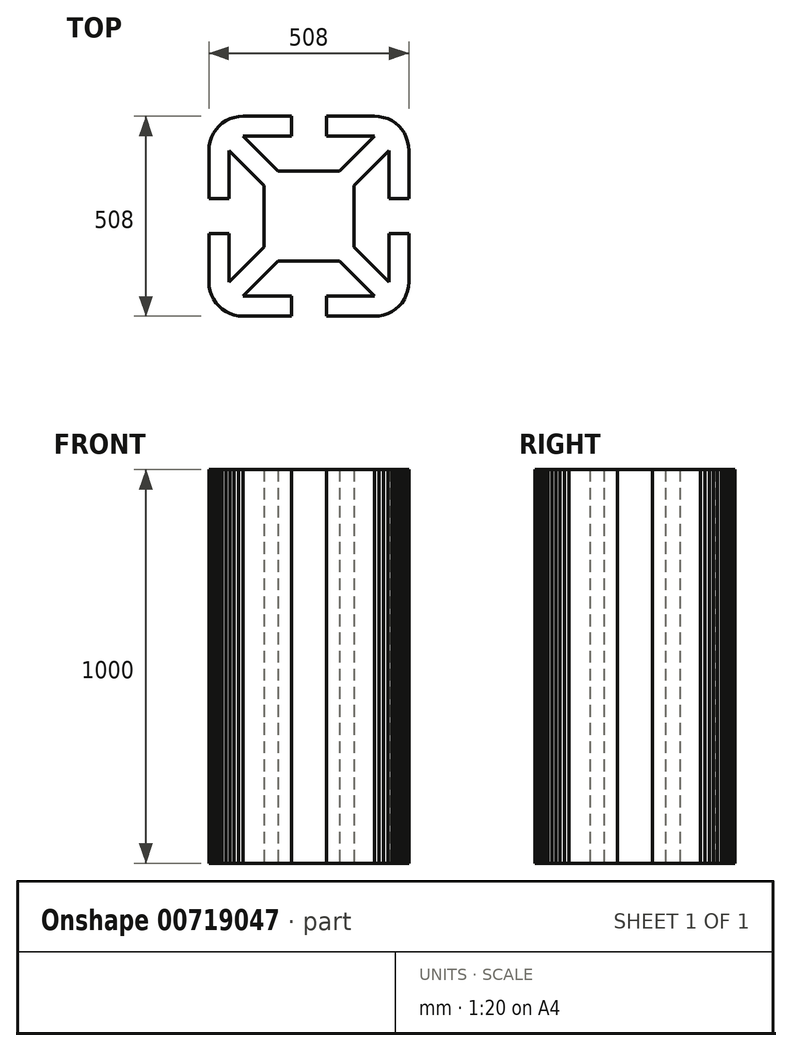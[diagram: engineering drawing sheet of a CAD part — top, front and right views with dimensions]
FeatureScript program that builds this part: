
annotation { "Feature Type Name" : "Feature", "Feature Type Description" : "" }
export const myFeature = defineFeature(function(context is Context, id is Id, definition is map)
    precondition{}
    {
        {
            var Q0;
            Q0=qCreatedBy(makeId("Top.planeOp"),FACE);
            var sketch = newSketch(context, id + "F0", { "sketchPlane" : qUnion([Q0])});
            skLineSegment(sketch, "E0", {"start": v(-251.05, 189.72) * mm, "end": v(-253.26, 178.6) * mm});
            skLineSegment(sketch, "E1", {"start": v(-247.4, 200.47) * mm, "end": v(-251.05, 189.72) * mm});
            skLineSegment(sketch, "E2", {"start": v(-228.6, 228.6) * mm, "end": v(-236.08, 220.07) * mm});
            skLineSegment(sketch, "E3", {"start": v(-220.07, 236.08) * mm, "end": v(-228.6, 228.6) * mm});
            skLineSegment(sketch, "E4", {"start": v(-210.64, 242.38) * mm, "end": v(-220.07, 236.08) * mm});
            skLineSegment(sketch, "E5", {"start": v(-167.28, 254) * mm, "end": v(-178.6, 253.26) * mm});
            skLineSegment(sketch, "E6", {"start": v(-167.28, 254) * mm, "end": v(-165.25, 254) * mm});
            skLineSegment(sketch, "E7", {"start": v(-165.25, 254) * mm, "end": v(-44.45, 254) * mm});
            skLineSegment(sketch, "E8", {"start": v(167.28, 203.2) * mm, "end": v(44.45, 203.2) * mm});
            skLineSegment(sketch, "E9", {"start": v(44.45, 254) * mm, "end": v(167.28, 254) * mm});
            skLineSegment(sketch, "E10", {"start": v(178.6, 253.26) * mm, "end": v(167.28, 254) * mm});
            skLineSegment(sketch, "E11", {"start": v(189.72, 251.05) * mm, "end": v(178.6, 253.26) * mm});
            skLineSegment(sketch, "E12", {"start": v(200.47, 247.4) * mm, "end": v(189.72, 251.05) * mm});
            skLineSegment(sketch, "E13", {"start": v(210.64, 242.38) * mm, "end": v(200.47, 247.4) * mm});
            skLineSegment(sketch, "E14", {"start": v(220.07, 236.08) * mm, "end": v(210.64, 242.38) * mm});
            skLineSegment(sketch, "E15", {"start": v(228.6, 228.6) * mm, "end": v(220.07, 236.08) * mm});
            skLineSegment(sketch, "E16", {"start": v(236.08, 220.07) * mm, "end": v(228.6, 228.6) * mm});
            skLineSegment(sketch, "E17", {"start": v(242.38, 210.64) * mm, "end": v(236.08, 220.07) * mm});
            skLineSegment(sketch, "E18", {"start": v(247.4, 200.47) * mm, "end": v(242.38, 210.64) * mm});
            skLineSegment(sketch, "E19", {"start": v(251.05, 189.72) * mm, "end": v(247.4, 200.47) * mm});
            skLineSegment(sketch, "E20", {"start": v(253.26, 178.6) * mm, "end": v(251.05, 189.72) * mm});
            skLineSegment(sketch, "E21", {"start": v(254, 167.28) * mm, "end": v(254, 44.45) * mm});
            skLineSegment(sketch, "E22", {"start": v(203.2, 44.45) * mm, "end": v(254, 44.45) * mm});
            skLineSegment(sketch, "E23", {"start": v(203.2, 44.45) * mm, "end": v(203.2, 167.28) * mm});
            skLineSegment(sketch, "E24", {"start": v(114.3, 78.38) * mm, "end": v(203.2, 167.28) * mm});
            skLineSegment(sketch, "E25", {"start": v(114.3, -78.38) * mm, "end": v(114.3, 78.38) * mm});
            skLineSegment(sketch, "E26", {"start": v(203.2, -167.28) * mm, "end": v(114.3, -78.38) * mm});
            skLineSegment(sketch, "E27", {"start": v(203.2, -167.28) * mm, "end": v(203.2, -44.45) * mm});
            skLineSegment(sketch, "E28", {"start": v(203.2, -44.45) * mm, "end": v(254, -44.45) * mm});
            skLineSegment(sketch, "E29", {"start": v(254, -44.45) * mm, "end": v(254, -167.28) * mm});
            skLineSegment(sketch, "E30", {"start": v(251.05, -189.72) * mm, "end": v(253.26, -178.6) * mm});
            skLineSegment(sketch, "E31", {"start": v(247.4, -200.47) * mm, "end": v(251.05, -189.72) * mm});
            skLineSegment(sketch, "E32", {"start": v(242.38, -210.64) * mm, "end": v(247.4, -200.47) * mm});
            skLineSegment(sketch, "E33", {"start": v(236.08, -220.07) * mm, "end": v(242.38, -210.64) * mm});
            skLineSegment(sketch, "E34", {"start": v(220.07, -236.08) * mm, "end": v(228.6, -228.6) * mm});
            skLineSegment(sketch, "E35", {"start": v(210.64, -242.38) * mm, "end": v(220.07, -236.08) * mm});
            skLineSegment(sketch, "E36", {"start": v(200.47, -247.4) * mm, "end": v(210.64, -242.38) * mm});
            skLineSegment(sketch, "E37", {"start": v(189.72, -251.05) * mm, "end": v(200.47, -247.4) * mm});
            skLineSegment(sketch, "E38", {"start": v(178.6, -253.26) * mm, "end": v(189.72, -251.05) * mm});
            skLineSegment(sketch, "E39", {"start": v(167.28, -254) * mm, "end": v(44.45, -254) * mm});
            skLineSegment(sketch, "E40", {"start": v(44.45, -203.2) * mm, "end": v(44.45, -254) * mm});
            skLineSegment(sketch, "E41", {"start": v(44.45, -203.2) * mm, "end": v(167.28, -203.2) * mm});
            skLineSegment(sketch, "E42", {"start": v(78.38, -114.3) * mm, "end": v(167.28, -203.2) * mm});
            skLineSegment(sketch, "E43", {"start": v(-78.38, -114.3) * mm, "end": v(78.38, -114.3) * mm});
            skLineSegment(sketch, "E44", {"start": v(-167.28, -203.2) * mm, "end": v(-78.38, -114.3) * mm});
            skLineSegment(sketch, "E45", {"start": v(-167.28, -203.2) * mm, "end": v(-44.45, -203.2) * mm});
            skLineSegment(sketch, "E46", {"start": v(-44.45, -203.2) * mm, "end": v(-44.45, -254) * mm});
            skLineSegment(sketch, "E47", {"start": v(-44.45, -254) * mm, "end": v(-167.28, -254) * mm});
            skLineSegment(sketch, "E48", {"start": v(-178.6, -253.26) * mm, "end": v(-167.28, -254) * mm});
            skLineSegment(sketch, "E49", {"start": v(-189.72, -251.05) * mm, "end": v(-178.6, -253.26) * mm});
            skLineSegment(sketch, "E50", {"start": v(-200.47, -247.4) * mm, "end": v(-189.72, -251.05) * mm});
            skLineSegment(sketch, "E51", {"start": v(-210.64, -242.38) * mm, "end": v(-200.47, -247.4) * mm});
            skLineSegment(sketch, "E52", {"start": v(-220.07, -236.08) * mm, "end": v(-210.64, -242.38) * mm});
            skLineSegment(sketch, "E53", {"start": v(-247.4, -200.47) * mm, "end": v(-242.38, -210.64) * mm});
            skLineSegment(sketch, "E54", {"start": v(-251.05, -189.72) * mm, "end": v(-247.4, -200.47) * mm});
            skLineSegment(sketch, "E55", {"start": v(-253.26, -178.6) * mm, "end": v(-251.05, -189.72) * mm});
            skLineSegment(sketch, "E56", {"start": v(-254, -167.28) * mm, "end": v(-253.26, -178.6) * mm});
            skLineSegment(sketch, "E57", {"start": v(-254, -167.28) * mm, "end": v(-254, -44.45) * mm});
            skLineSegment(sketch, "E58", {"start": v(-203.2, -44.45) * mm, "end": v(-254, -44.45) * mm});
            skLineSegment(sketch, "E59", {"start": v(-203.2, -44.45) * mm, "end": v(-203.2, -167.28) * mm});
            skLineSegment(sketch, "E60", {"start": v(-114.3, 78.38) * mm, "end": v(-114.3, -78.38) * mm});
            skLineSegment(sketch, "E61", {"start": v(-203.2, 167.28) * mm, "end": v(-114.3, 78.38) * mm});
            skLineSegment(sketch, "E62", {"start": v(-203.2, 167.28) * mm, "end": v(-203.2, 44.45) * mm});
            skLineSegment(sketch, "E63", {"start": v(-254, 44.45) * mm, "end": v(-254, 167.28) * mm});
            skLineSegment(sketch, "E64", {"start": v(-203.2, 44.45) * mm, "end": v(-254, 44.45) * mm});
            skLineSegment(sketch, "E65", {"start": v(-242.38, 210.64) * mm, "end": v(-247.4, 200.47) * mm});
            skLineSegment(sketch, "E66", {"start": v(-114.3, -78.38) * mm, "end": v(-203.2, -167.28) * mm});
            skLineSegment(sketch, "E67", {"start": v(-236.08, 220.07) * mm, "end": v(-242.38, 210.64) * mm});
            skLineSegment(sketch, "E68", {"start": v(-253.26, 178.6) * mm, "end": v(-254, 167.28) * mm});
            skLineSegment(sketch, "E69", {"start": v(167.28, -254) * mm, "end": v(178.6, -253.26) * mm});
            skLineSegment(sketch, "E70", {"start": v(-228.6, -228.6) * mm, "end": v(-220.07, -236.08) * mm});
            skLineSegment(sketch, "E71", {"start": v(-236.08, -220.07) * mm, "end": v(-228.6, -228.6) * mm});
            skLineSegment(sketch, "E72", {"start": v(-78.38, 114.3) * mm, "end": v(-167.28, 203.2) * mm});
            skLineSegment(sketch, "E73", {"start": v(-242.38, -210.64) * mm, "end": v(-236.08, -220.07) * mm});
            skLineSegment(sketch, "E74", {"start": v(78.38, 114.3) * mm, "end": v(-78.38, 114.3) * mm});
            skLineSegment(sketch, "E75", {"start": v(-44.45, 203.2) * mm, "end": v(-167.28, 203.2) * mm});
            skLineSegment(sketch, "E76", {"start": v(167.28, 203.2) * mm, "end": v(78.38, 114.3) * mm});
            skLineSegment(sketch, "E77", {"start": v(44.45, 203.2) * mm, "end": v(44.45, 254) * mm});
            skLineSegment(sketch, "E78", {"start": v(-189.72, 251.05) * mm, "end": v(-200.47, 247.4) * mm});
            skLineSegment(sketch, "E79", {"start": v(-178.6, 253.26) * mm, "end": v(-189.72, 251.05) * mm});
            skLineSegment(sketch, "E80", {"start": v(254, 167.28) * mm, "end": v(253.26, 178.6) * mm});
            skLineSegment(sketch, "E81", {"start": v(-44.45, 203.2) * mm, "end": v(-44.45, 254) * mm});
            skLineSegment(sketch, "E82", {"start": v(-200.47, 247.4) * mm, "end": v(-210.64, 242.38) * mm});
            skLineSegment(sketch, "E83", {"start": v(253.26, -178.6) * mm, "end": v(254, -167.28) * mm});
            skLineSegment(sketch, "E84", {"start": v(228.6, -228.6) * mm, "end": v(236.08, -220.07) * mm});
            skSolve(sketch);
        }
        {
            var Q0;
            Q0 = qSketchRegion(id + "F0", true);
            extrude(context, id + "F1", {"entities" : qUnion([Q0]), "depth" : 1000 * mm, "offsetDistance" : 25.4 * mm});
        }
    });
